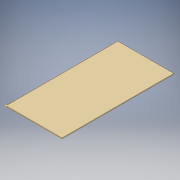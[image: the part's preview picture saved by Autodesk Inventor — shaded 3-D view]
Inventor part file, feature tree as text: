
AUTODESK INVENTOR PART (.ipt)
format: ipt  version: 2018 (Build 220112000, 112)  size: 109,568 bytes
history: native  units: in
note: dims shown in document units (in); Inventor stores cm internally (conversion verified against a paired STEP export)
features: sketch x2, extrude x1
ambient origin geometry x8: Origin, YZ Plane, XZ Plane, XY Plane, X Axis, Y Axis, Z Axis, Center Point
bodies: Solid1 (feature_tree)
feature tree (3):
  extrude  "Extrusion1"  Depth=1440.0in
  sketch  "Sketch2"  dims[d2=10.0in d3=0.0in]
  sketch  "Sketch1"  dims[d0=720.0in d1=1440.0in]
